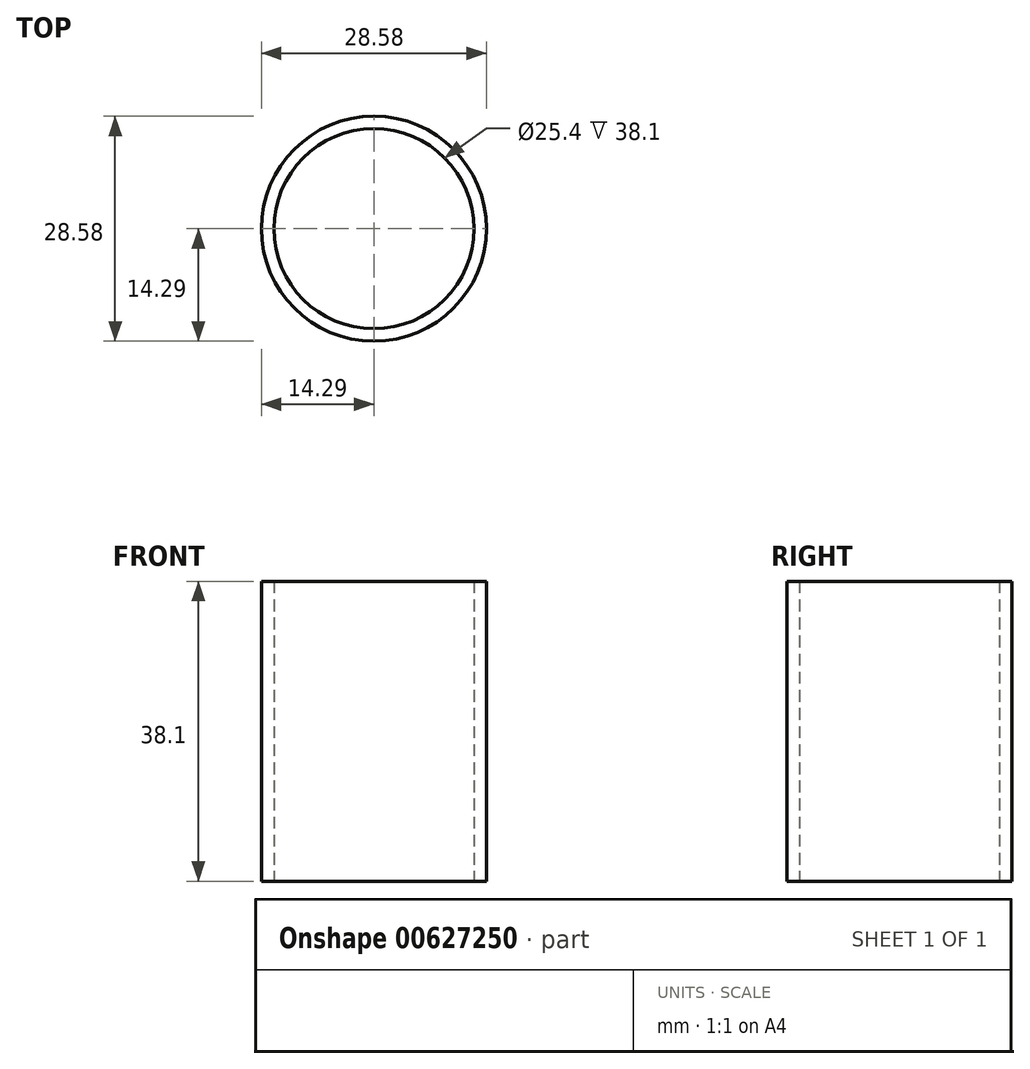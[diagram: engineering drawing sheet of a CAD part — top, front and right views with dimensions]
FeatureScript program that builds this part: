
annotation { "Feature Type Name" : "Feature", "Feature Type Description" : "" }
export const myFeature = defineFeature(function(context is Context, id is Id, definition is map)
    precondition{}
    {
        {
            var Q0;
            Q0=qCreatedBy(makeId("Top.planeOp"),FACE);
            var sketch = newSketch(context, id + "F0", { "sketchPlane" : qUnion([Q0])});
            skLineSegment(sketch, "E0", {"start": v(0, 0) * mm, "end": v(12.7, 0) * mm});
            skCircle(sketch, "E1", {"center": v(0, 0) * mm, "radius": 12.7 * mm});
            skCircle(sketch, "E2.0", {"center": v(0, 0) * mm, "radius": 14.29 * mm});
            skSolve(sketch);
        }
        {
            var Q0;
            Q0=qCreatedBy(makeId("Top.planeOp"),FACE);
            var sketch = newSketch(context, id + "F1", { "sketchPlane" : qUnion([Q0])});
            skSolve(sketch);
        }
        {
            var Q0;
            Q0=qSketchRegion(id+"F1",true);
            var Q1;
            Q1=makeQuery(id+"F0.imprint","IMPRINT",FACE,{"disambiguationData":[TD([[makeQuery(id+"F0.imprint","IMPRINT",EDGE,{"derivedFrom":sQuery(id+"F0.wireOp",EDGE,"E1")}),-1.0]])]});
            extrude(context, id + "F2", {"entities" : qUnion([Q0, Q1]), "depth" : 38.1 * mm, "offsetDistance" : 25.4 * mm});
        }
    });
